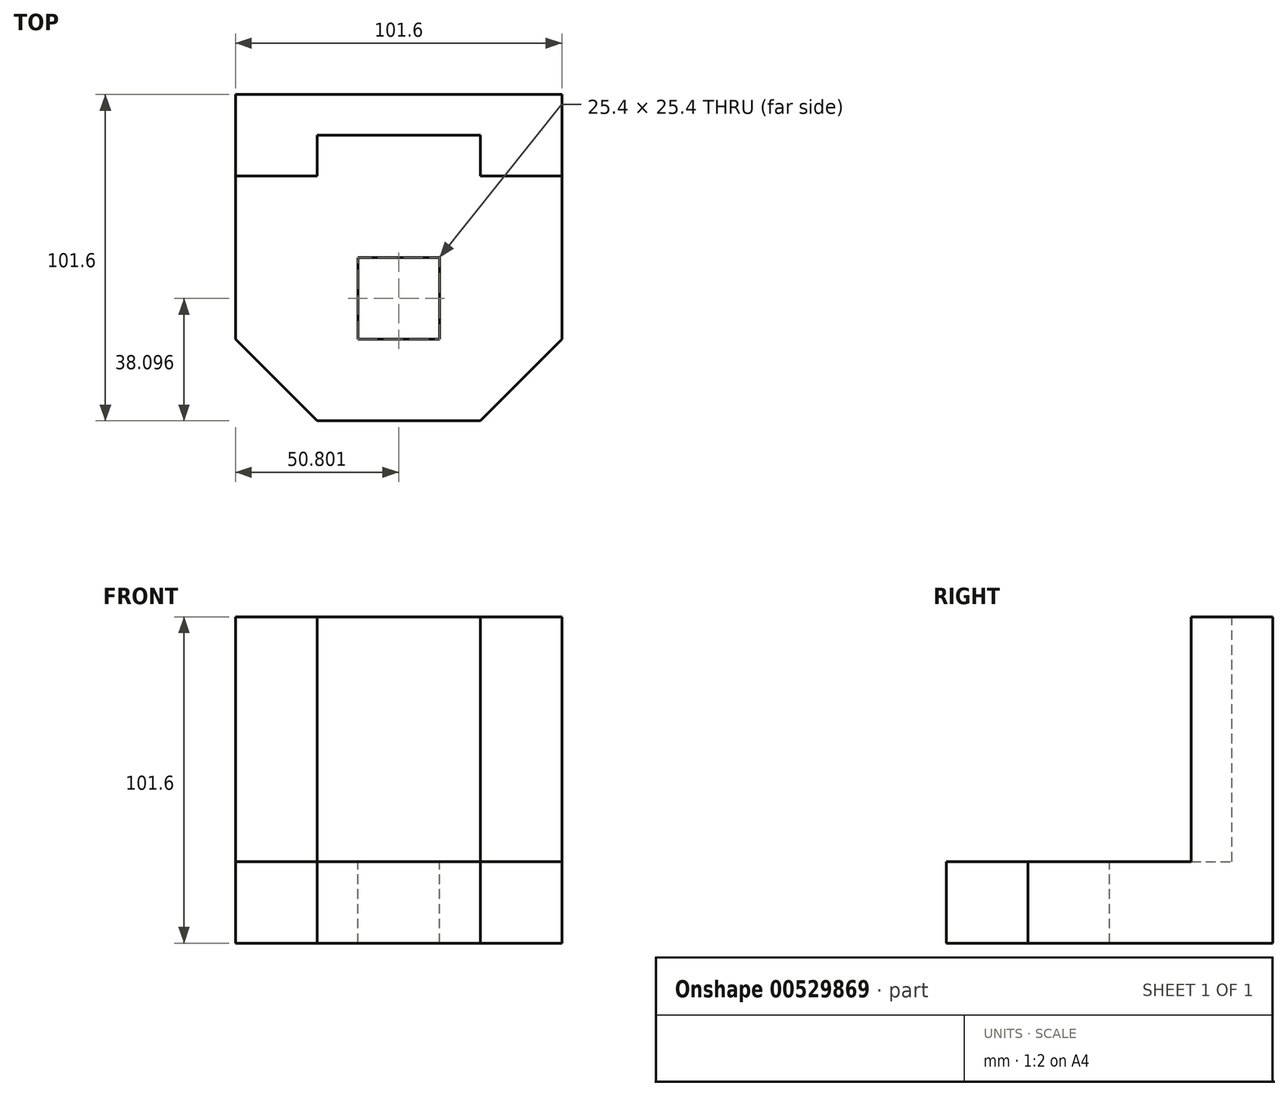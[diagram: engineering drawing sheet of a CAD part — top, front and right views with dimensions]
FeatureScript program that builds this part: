
annotation { "Feature Type Name" : "Feature", "Feature Type Description" : "" }
export const myFeature = defineFeature(function(context is Context, id is Id, definition is map)
    precondition{}
    {
        {
            var Q0;
            Q0=qCreatedBy(makeId("Top.planeOp"),FACE);
            var sketch = newSketch(context, id + "F0", { "sketchPlane" : qUnion([Q0])});
            skLineSegment(sketch, "E0.bottom", {"start": v(-50.88, 62.3) * mm, "end": v(50.72, 62.3) * mm});
            skLineSegment(sketch, "E0.top", {"start": v(-50.88, -39.3) * mm, "end": v(50.72, -39.3) * mm});
            skLineSegment(sketch, "E0.left", {"start": v(-50.88, 62.3) * mm, "end": v(-50.88, -39.3) * mm});
            skLineSegment(sketch, "E0.right", {"start": v(50.72, 62.3) * mm, "end": v(50.72, -39.3) * mm});
            skSolve(sketch);
        }
        {
            var Q0;
            Q0=makeQuery(id+"F0.imprint","IMPRINT",FACE,{"disambiguationData":[TD([[makeQuery(id+"F0.imprint","IMPRINT",EDGE,{"derivedFrom":sQuery(id+"F0.wireOp",EDGE,"E0.bottom")}),-1.0]])]});
            extrude(context, id + "F1", {"entities" : qUnion([Q0]), "depth" : 101.6 * mm, "offsetDistance" : 25.4 * mm});
        }
        {
            var Q0;
            Q0=makeQuery(id+"F1.opExtrude","CAP_FACE",FACE,{"disambiguationData":[OSD([sQuery(id+"F0.wireOp",EDGE,"E0.bottom"),sQuery(id+"F0.wireOp",EDGE,"E0.top"),sQuery(id+"F0.wireOp",EDGE,"E0.left"),sQuery(id+"F0.wireOp",EDGE,"E0.right")])],"isStart":false});
            var sketch = newSketch(context, id + "F2", { "sketchPlane" : qUnion([Q0])});
            skLineSegment(sketch, "E1.bottom", {"start": v(-50.88, -39.3) * mm, "end": v(50.72, -39.3) * mm});
            skLineSegment(sketch, "E1.top", {"start": v(-50.88, 36.9) * mm, "end": v(50.72, 36.9) * mm});
            skLineSegment(sketch, "E1.left", {"start": v(-50.88, -39.3) * mm, "end": v(-50.88, 36.9) * mm});
            skLineSegment(sketch, "E1.right", {"start": v(50.72, -39.3) * mm, "end": v(50.72, 36.9) * mm});
            skSolve(sketch);
        }
        {
            var Q0;
            Q0=makeQuery(id+"F2.imprint","IMPRINT",FACE,{"disambiguationData":[TD([[makeQuery(id+"F2.imprint","IMPRINT",EDGE,{"derivedFrom":sQuery(id+"F2.wireOp",EDGE,"E1.bottom")}),1.0]])]});
            extrude(context, id + "F3", {"entities" : qUnion([Q0]), "operationType" : NewBodyOperationType.REMOVE, "oppositeDirection" : true, "depth" : 76.2 * mm, "offsetDistance" : 25.4 * mm});
        }
        {
            var Q0;
            Q0=makeQuery(id+"F1.opExtrude","CAP_FACE",FACE,{"disambiguationData":[OSD([sQuery(id+"F0.wireOp",EDGE,"E0.bottom"),sQuery(id+"F0.wireOp",EDGE,"E0.top"),sQuery(id+"F0.wireOp",EDGE,"E0.left"),sQuery(id+"F0.wireOp",EDGE,"E0.right")])],"isStart":false});
            var sketch = newSketch(context, id + "F4", { "sketchPlane" : qUnion([Q0])});
            skLineSegment(sketch, "E2.bottom", {"start": v(50.72, 36.9) * mm, "end": v(25.32, 36.9) * mm});
            skLineSegment(sketch, "E2.top", {"start": v(50.72, 49.6) * mm, "end": v(25.32, 49.6) * mm});
            skLineSegment(sketch, "E2.left", {"start": v(50.72, 36.9) * mm, "end": v(50.72, 49.6) * mm});
            skLineSegment(sketch, "E2.right", {"start": v(25.32, 36.9) * mm, "end": v(25.32, 49.6) * mm});
            skLineSegment(sketch, "E3.bottom", {"start": v(-50.88, 36.9) * mm, "end": v(-38.18, 36.9) * mm});
            skLineSegment(sketch, "E3.top", {"start": v(-50.88, 49.6) * mm, "end": v(-38.18, 49.6) * mm});
            skLineSegment(sketch, "E3.left", {"start": v(-50.88, 36.9) * mm, "end": v(-50.88, 49.6) * mm});
            skLineSegment(sketch, "E3.right", {"start": v(-38.18, 36.9) * mm, "end": v(-38.18, 49.6) * mm});
            skLineSegment(sketch, "E4.bottom", {"start": v(-50.88, 36.9) * mm, "end": v(-25.48, 36.9) * mm});
            skLineSegment(sketch, "E4.top", {"start": v(-50.88, 49.6) * mm, "end": v(-25.48, 49.6) * mm});
            skLineSegment(sketch, "E4.right", {"start": v(-25.48, 36.9) * mm, "end": v(-25.48, 49.6) * mm});
            skLineSegment(sketch, "E5.bottom", {"start": v(-25.48, 49.6) * mm, "end": v(25.32, 49.6) * mm});
            skLineSegment(sketch, "E5.top", {"start": v(-25.48, 36.9) * mm, "end": v(25.32, 36.9) * mm});
            skLineSegment(sketch, "E5.left", {"start": v(-25.48, 49.6) * mm, "end": v(-25.48, 36.9) * mm});
            skLineSegment(sketch, "E5.right", {"start": v(25.32, 49.6) * mm, "end": v(25.32, 36.9) * mm});
            skSolve(sketch);
        }
        {
            var Q0;
            Q0=makeQuery(id+"F4.imprint","IMPRINT",FACE,{"disambiguationData":[TD([[makeQuery(id+"F4.imprint","IMPRINT",EDGE,{"derivedFrom":sQuery(id+"F4.wireOp",EDGE,"E5.bottom")}),-1.0]])]});
            extrude(context, id + "F5", {"entities" : qUnion([Q0]), "operationType" : NewBodyOperationType.REMOVE, "oppositeDirection" : true, "depth" : 76.2 * mm, "offsetDistance" : 25.4 * mm});
        }
        {
            var Q0;
            Q0=makeQuery(id+"F5.boolean.opBoolean","MERGE",FACE,{"derivedFrom":[makeQuery(id+"F3.boolean.opBoolean","COPY",FACE,{"derivedFrom":makeQuery(id+"F3.opExtrude","CAP_FACE",FACE,{"disambiguationData":[OSD([sQuery(id+"F2.wireOp",EDGE,"E1.bottom"),sQuery(id+"F2.wireOp",EDGE,"E1.top"),sQuery(id+"F2.wireOp",EDGE,"E1.left"),sQuery(id+"F2.wireOp",EDGE,"E1.right")])],"isStart":false})}),makeQuery(id+"F5.opExtrude","CAP_FACE",FACE,{"disambiguationData":[OSD([sQuery(id+"F4.wireOp",EDGE,"E5.bottom"),sQuery(id+"F4.wireOp",EDGE,"E5.top"),sQuery(id+"F4.wireOp",EDGE,"E5.left"),sQuery(id+"F4.wireOp",EDGE,"E5.right")])],"isStart":false})]});
            var sketch = newSketch(context, id + "F6", { "sketchPlane" : qUnion([Q0])});
            skLineSegment(sketch, "E6.bottom", {"start": v(-50.88, -39.3) * mm, "end": v(50.72, -39.3) * mm});
            skLineSegment(sketch, "E6.top", {"start": v(-50.88, -13.9) * mm, "end": v(50.72, -13.9) * mm});
            skLineSegment(sketch, "E6.left", {"start": v(-50.88, -39.3) * mm, "end": v(-50.88, -13.9) * mm});
            skLineSegment(sketch, "E6.right", {"start": v(50.72, -39.3) * mm, "end": v(50.72, -13.9) * mm});
            skLineSegment(sketch, "E7.bottom", {"start": v(-50.88, -13.9) * mm, "end": v(-12.78, -13.9) * mm});
            skLineSegment(sketch, "E7.top", {"start": v(-50.88, 11.5) * mm, "end": v(-12.78, 11.5) * mm});
            skLineSegment(sketch, "E7.left", {"start": v(-50.88, -13.9) * mm, "end": v(-50.88, 11.5) * mm});
            skLineSegment(sketch, "E7.right", {"start": v(-12.78, -13.9) * mm, "end": v(-12.78, 11.5) * mm});
            skLineSegment(sketch, "E8.bottom", {"start": v(50.72, -13.9) * mm, "end": v(12.62, -13.9) * mm});
            skLineSegment(sketch, "E8.top", {"start": v(50.72, 11.5) * mm, "end": v(12.62, 11.5) * mm});
            skLineSegment(sketch, "E8.left", {"start": v(50.72, -13.9) * mm, "end": v(50.72, 11.5) * mm});
            skLineSegment(sketch, "E8.right", {"start": v(12.62, -13.9) * mm, "end": v(12.62, 11.5) * mm});
            skLineSegment(sketch, "E9.bottom", {"start": v(12.62, 11.5) * mm, "end": v(-12.78, 11.5) * mm});
            skLineSegment(sketch, "E9.top", {"start": v(12.62, -13.9) * mm, "end": v(-12.78, -13.9) * mm});
            skLineSegment(sketch, "E9.left", {"start": v(12.62, 11.5) * mm, "end": v(12.62, -13.9) * mm});
            skLineSegment(sketch, "E9.right", {"start": v(-12.78, 11.5) * mm, "end": v(-12.78, -13.9) * mm});
            skSolve(sketch);
        }
        {
            var Q0;
            Q0=makeQuery(id+"F6.imprint","IMPRINT",FACE,{"disambiguationData":[TD([[makeQuery(id+"F6.imprint","IMPRINT",EDGE,{"derivedFrom":sQuery(id+"F6.wireOp",EDGE,"E9.bottom")}),1.0]])]});
            extrude(context, id + "F7", {"entities" : qUnion([Q0]), "operationType" : NewBodyOperationType.REMOVE, "oppositeDirection" : true, "depth" : 75.44 * mm, "offsetDistance" : 25.4 * mm});
        }
        {
            var Q0;
            Q0=makeQuery(id+"F5.boolean.opBoolean","MERGE",FACE,{"derivedFrom":[makeQuery(id+"F3.boolean.opBoolean","COPY",FACE,{"derivedFrom":makeQuery(id+"F3.opExtrude","CAP_FACE",FACE,{"disambiguationData":[OSD([sQuery(id+"F2.wireOp",EDGE,"E1.bottom"),sQuery(id+"F2.wireOp",EDGE,"E1.top"),sQuery(id+"F2.wireOp",EDGE,"E1.left"),sQuery(id+"F2.wireOp",EDGE,"E1.right")])],"isStart":false})}),makeQuery(id+"F5.opExtrude","CAP_FACE",FACE,{"disambiguationData":[OSD([sQuery(id+"F4.wireOp",EDGE,"E5.bottom"),sQuery(id+"F4.wireOp",EDGE,"E5.top"),sQuery(id+"F4.wireOp",EDGE,"E5.left"),sQuery(id+"F4.wireOp",EDGE,"E5.right")])],"isStart":false})]});
            var sketch = newSketch(context, id + "F8", { "sketchPlane" : qUnion([Q0])});
            skLineSegment(sketch, "E10.bottom", {"start": v(-50.88, -39.3) * mm, "end": v(-25.48, -39.3) * mm});
            skLineSegment(sketch, "E10.top", {"start": v(-50.88, -13.9) * mm, "end": v(-25.48, -13.9) * mm});
            skLineSegment(sketch, "E10.left", {"start": v(-50.88, -39.3) * mm, "end": v(-50.88, -13.9) * mm});
            skLineSegment(sketch, "E10.right", {"start": v(-25.48, -39.3) * mm, "end": v(-25.48, -13.9) * mm});
            skLineSegment(sketch, "E11.bottom", {"start": v(50.72, -39.3) * mm, "end": v(25.32, -39.3) * mm});
            skLineSegment(sketch, "E11.top", {"start": v(50.72, -13.9) * mm, "end": v(25.32, -13.9) * mm});
            skLineSegment(sketch, "E11.left", {"start": v(50.72, -39.3) * mm, "end": v(50.72, -13.9) * mm});
            skLineSegment(sketch, "E11.right", {"start": v(25.32, -39.3) * mm, "end": v(25.32, -13.9) * mm});
            skLineSegment(sketch, "E12", {"start": v(-50.88, -13.9) * mm, "end": v(-25.48, -39.3) * mm});
            skLineSegment(sketch, "E13", {"start": v(25.32, -39.3) * mm, "end": v(50.72, -13.9) * mm});
            skSolve(sketch);
        }
        {
            var Q0;
            Q0=makeQuery(id+"F8.imprint","IMPRINT",FACE,{"disambiguationData":[TD([[makeQuery(id+"F8.imprint","IMPRINT",EDGE,{"derivedFrom":sQuery(id+"F8.wireOp",EDGE,"E10.bottom")}),1.0]])]});
            var Q1;
            Q1=makeQuery(id+"F8.imprint","IMPRINT",FACE,{"disambiguationData":[TD([[makeQuery(id+"F8.imprint","IMPRINT",EDGE,{"derivedFrom":sQuery(id+"F8.wireOp",EDGE,"E11.bottom")}),1.0]])]});
            extrude(context, id + "F9", {"entities" : qUnion([Q0, Q1]), "operationType" : NewBodyOperationType.REMOVE, "oppositeDirection" : true, "depth" : 57.9 * mm, "offsetDistance" : 25.4 * mm});
        }
    });
